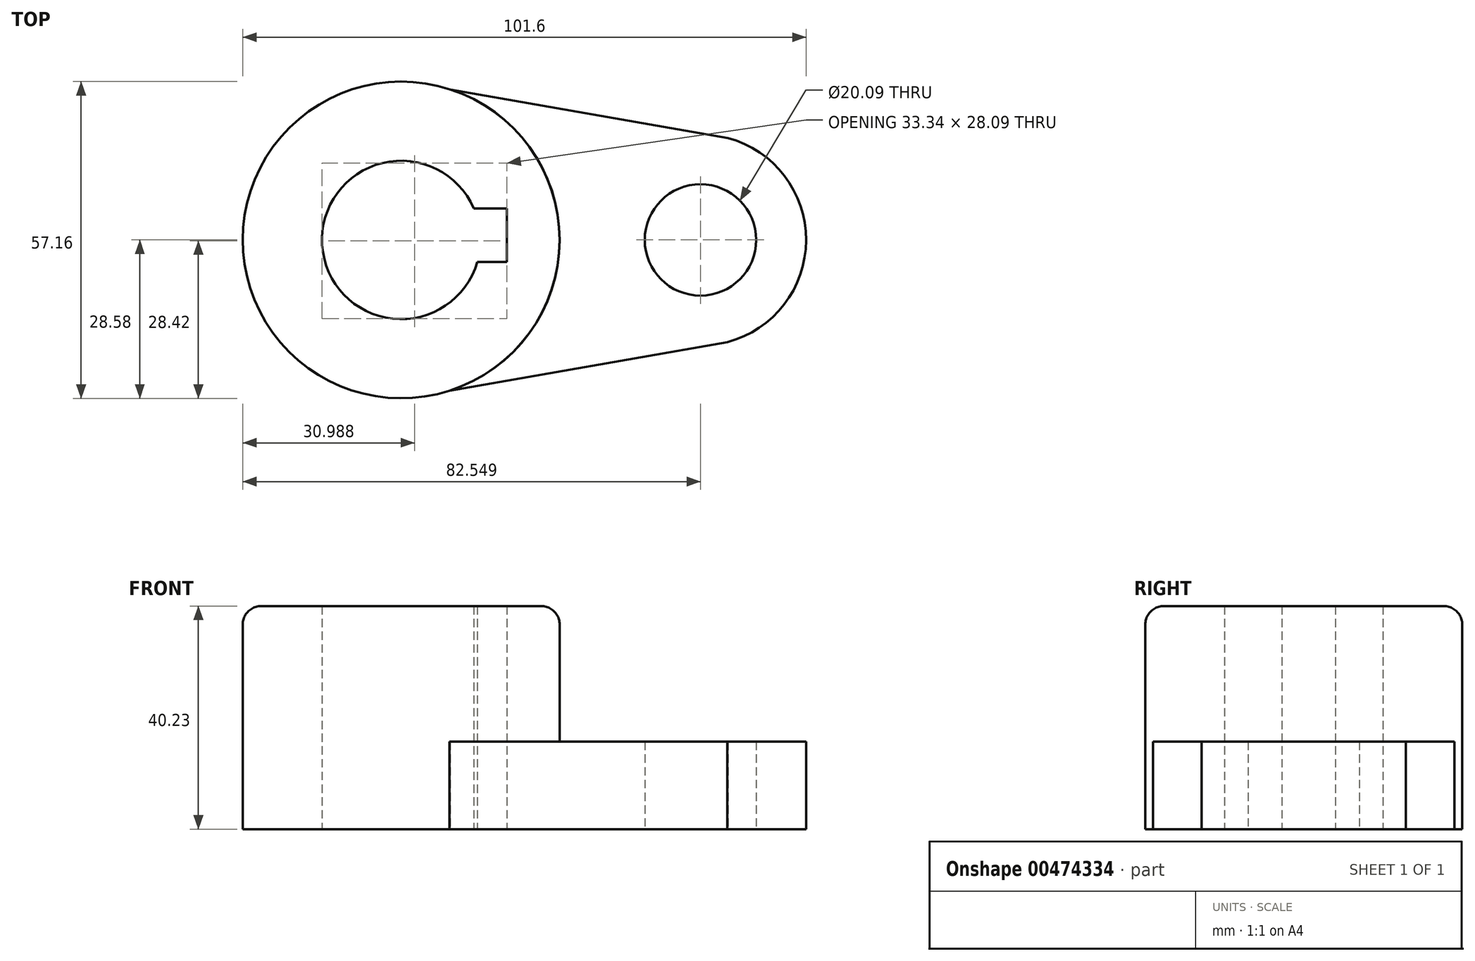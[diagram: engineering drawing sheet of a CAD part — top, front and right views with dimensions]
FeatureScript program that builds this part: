
annotation { "Feature Type Name" : "Feature", "Feature Type Description" : "" }
export const myFeature = defineFeature(function(context is Context, id is Id, definition is map)
    precondition{}
    {
        {
            var Q0;
            Q0=qCreatedBy(makeId("Top.planeOp"),FACE);
            var sketch = newSketch(context, id + "F0", { "sketchPlane" : qUnion([Q0])});
            skCircle(sketch, "E0", {"center": v(-28.12, 0) * mm, "radius": 28.58 * mm});
            skArc(sketch, "E1", {"start": v(-15.02, 5.7) * mm, "mid": v(-42.37, -0.93) * mm, "end": v(-14.39, -3.95) * mm});
            skLineSegment(sketch, "E2.bottom", {"start": v(-14.39, -3.95) * mm, "end": v(-9.03, -3.95) * mm});
            skLineSegment(sketch, "E2.right", {"start": v(-9.03, -3.95) * mm, "end": v(-9.03, 5.7) * mm});
            skCircle(sketch, "E3", {"center": v(25.86, 0) * mm, "radius": 10.05 * mm});
            skArc(sketch, "E4", {"start": v(30.7, -18.42) * mm, "mid": v(44.9, -0.06) * mm, "end": v(30.82, 18.4) * mm});
            skLineSegment(sketch, "E5", {"start": v(30.82, 18.4) * mm, "end": v(-19.28, 27.17) * mm});
            skLineSegment(sketch, "E6", {"start": v(30.7, -18.42) * mm, "end": v(-19.4, -27.21) * mm});
            skLineSegment(sketch, "E7.trimOffspring", {"start": v(-15.02, 5.7) * mm, "end": v(-9.03, 5.7) * mm});
            skSolve(sketch);
        }
        {
            var Q0;
            Q0=makeQuery(id+"F0.imprint","IMPRINT",FACE,{"disambiguationData":[TD([[makeQuery(id+"F0.imprint","IMPRINT",EDGE,{"derivedFrom":sQuery(id+"F0.wireOp",EDGE,"E3")}),-1.0]])]});
            extrude(context, id + "F1", {"entities" : qUnion([Q0]), "depth" : 15.77 * mm});
        }
        {
            var Q0;
            Q0=makeQuery(id+"F0.imprint","IMPRINT",FACE,{"disambiguationData":[TD([[makeQuery(id+"F0.imprint","IMPRINT",EDGE,{"derivedFrom":sQuery(id+"F0.wireOp",EDGE,"E1")}),-1.0]])]});
            extrude(context, id + "F2", {"entities" : qUnion([Q0]), "operationType" : NewBodyOperationType.ADD, "depth" : 40.23 * mm});
        }
        {
            var Q0;
            Q0=makeQuery(id+"F2.opExtrude","CAP_EDGE",EDGE,{"disambiguationData":[OSD([sQuery(id+"F0.wireOp",EDGE,"E0")])],"isStart":false});
            fillet(context, id + "F3", {"entities" : qUnion([Q0]), "radius" : 3.3 * mm, "tangentPropagation" : true, "allowEdgeOverflow" : false});
        }
    });
